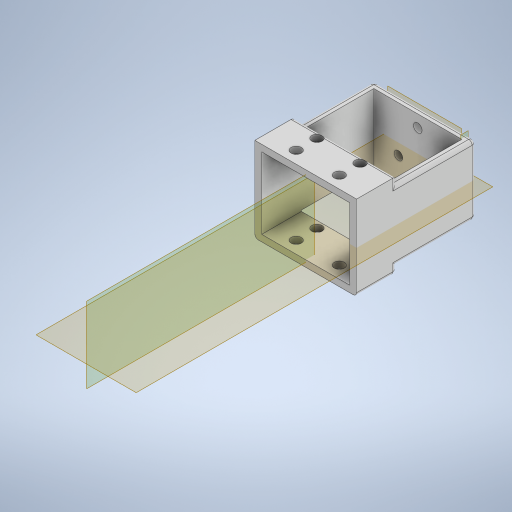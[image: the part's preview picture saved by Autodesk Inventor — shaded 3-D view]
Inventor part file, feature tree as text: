
AUTODESK INVENTOR PART (.ipt)
format: ipt  version: 2024 (Build 280153000, 153)  size: 856,064 bytes
history: native  units: mm
features: plane x5, extrude x5, sketch x5, other x5, reference x4, mirror x2, projected_geometry x2, fillet x1
ambient origin geometry x8: Origin, YZ Plane, XZ Plane, XY Plane, X Axis, Y Axis, Z Axis, Center Point
bodies: Solid1 (feature_tree)
feature tree (29):
  plane  "Work Plane1"
  plane  "Work Plane7"
  extrude  "Extrusion1"  Depth=4.5mm
  extrude  "Extrusion6"  TaperAngle=60.0deg  [1 undecoded]
  extrude  "Extrusion7"  Depth=41.5mm
  sketch  "Sketch8"  dims[d33=12.441343mm d34=8.5mm]
  plane  "Work Plane8"
  extrude  "Extrusion8"  Depth=8.5mm
  plane  "Work Plane9"
  plane  "Work Plane10"
  mirror  "Mirror3"
  mirror  "Mirror4"
  extrude  "Extrusion9"  Depth=2.0mm
  fillet  "Fillet4"  Radius=16.104137mm
  sketch  "Sketch1"  dims[d0=4.0mm d1=0.0mm d28=4.5mm]
  reference  "Reference1"
  reference  "Reference2"
  reference  "Reference3"
  sketch  "Sketch6"  dims[d29=40.0mm d30=60.0deg]
  projected_geometry  "Projected Loop4"
  sketch  "Sketch7"  dims[d31=40.0mm d32=41.5mm]
  projected_geometry  "Projected Loop5"
  sketch  "Sketch9"  dims[d35=4.120835mm d36=8.5mm d37=16.104137mm d38=8.5mm d39=16.104137mm d40=8.5mm d41=19.601597mm d42=4.0mm d43=4.0mm d44=0.0mm d45=0.0mm d46=65.0mm d47=0.0mm d48=23.0mm d49=4.5mm d50=0.0mm d51=3.8mm d52=4.5mm d53=0.0mm d54=1.0mm d55=1.0mm d56=1.0mm d57=1.0mm d58=0.0mm d59=0.0mm d60=1.0mm d61=1.0mm d62=1.0mm d63=2.0mm d6=0.5mm d7=0.872665mm d8=0.5mm d9=0.872665mm]
  reference  "Reference5"
  other  "<userpath>\Documents\Inventor\robot arm\gripper-adapter-as.iam"
  other  "gripper-adapter-as.iam"
  other  "ServoMount:1"
  other  "upper arm:1"
  other  "Assembly1"
note: 1 required parameter value undecoded (feature->parameter linkage not recoverable at this tier; creation-order binding heuristic only, values carry confidence <= 0.55)
